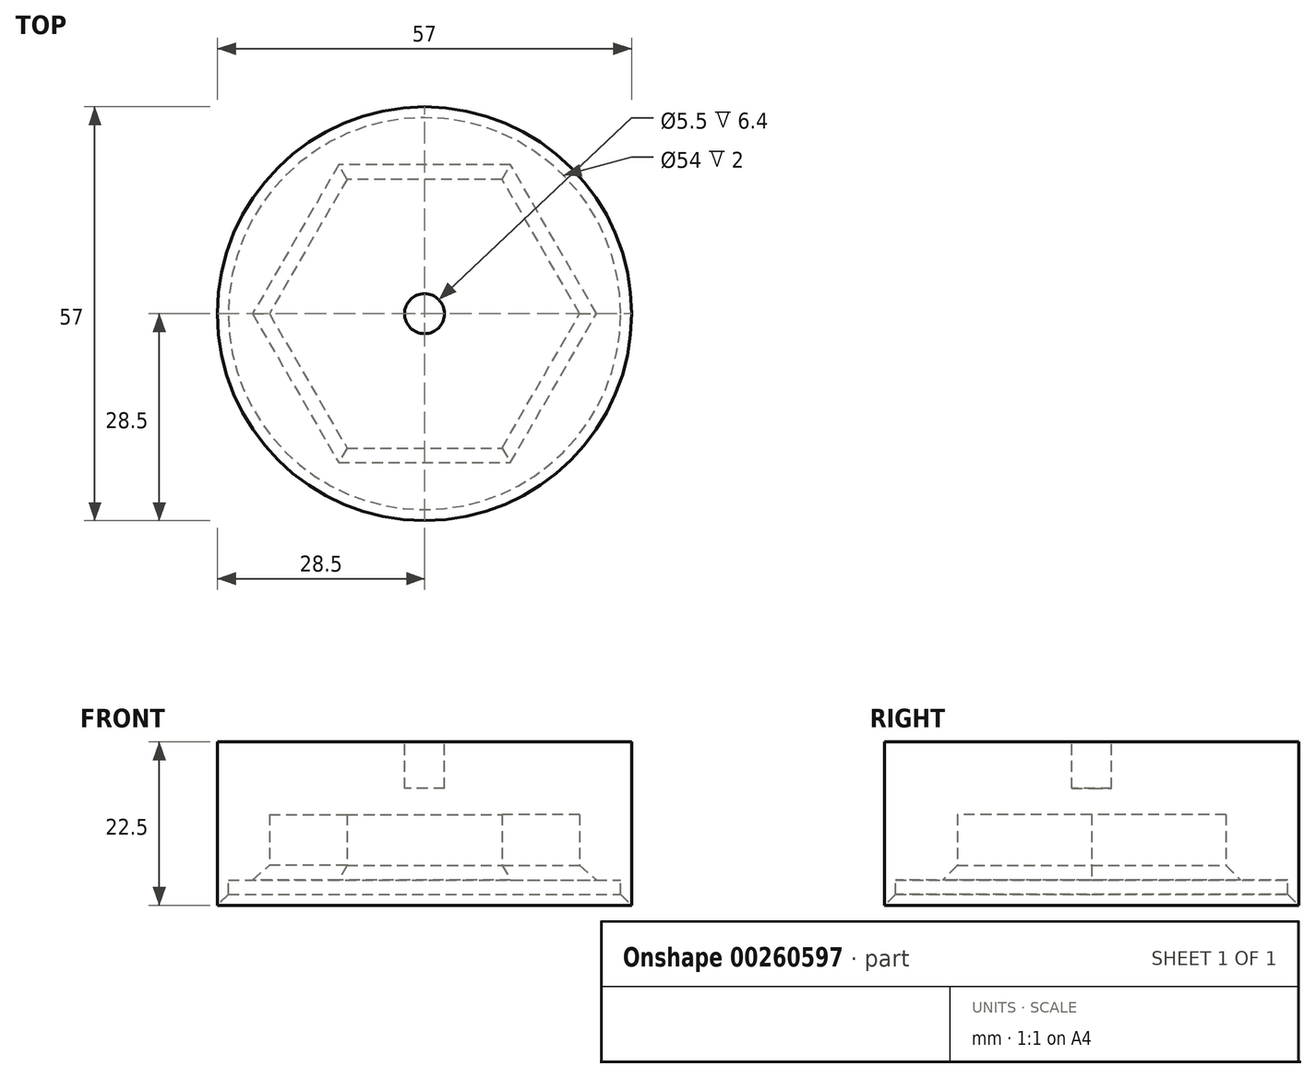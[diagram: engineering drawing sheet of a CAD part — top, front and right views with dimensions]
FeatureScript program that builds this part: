
annotation { "Feature Type Name" : "Feature", "Feature Type Description" : "" }
export const myFeature = defineFeature(function(context is Context, id is Id, definition is map)
    precondition{}
    {
        {
            var Q0;
            Q0=qCreatedBy(makeId("Top.planeOp"),FACE);
            var sketch = newSketch(context, id + "F0", { "sketchPlane" : qUnion([Q0])});
            skCircle(sketch, "E0", {"center": v(0, 0) * mm, "radius": 28.5 * mm});
            skSolve(sketch);
        }
        {
            var Q0;
            Q0=makeQuery(id+"F0.imprint","IMPRINT",FACE,{"disambiguationData":[TD([[makeQuery(id+"F0.imprint","IMPRINT",EDGE,{"derivedFrom":sQuery(id+"F0.wireOp",EDGE,"E0")}),1.0]])]});
            extrude(context, id + "F1", {"entities" : qUnion([Q0]), "depth" : 11 * mm, "offsetDistance" : 25 * mm});
        }
        {
            var Q0;
            Q0=makeQuery(id+"F1.opExtrude","CAP_FACE",FACE,{"disambiguationData":[OSD([sQuery(id+"F0.wireOp",EDGE,"E0")])],"isStart":true});
            var sketch = newSketch(context, id + "F2", { "sketchPlane" : qUnion([Q0])});
            skCircle(sketch, "E1.cCircle", {"center": v(0, 0) * mm, "radius": 18.5 * mm, "construction": true});
            skLineSegment(sketch, "E1.0", {"start": v(-10.68, 18.5) * mm, "end": v(10.68, 18.5) * mm});
            skLineSegment(sketch, "E1.1", {"start": v(10.68, 18.5) * mm, "end": v(21.36, 0) * mm});
            skLineSegment(sketch, "E1.2", {"start": v(21.36, 0) * mm, "end": v(10.68, -18.5) * mm});
            skLineSegment(sketch, "E1.3", {"start": v(10.68, -18.5) * mm, "end": v(-10.68, -18.5) * mm});
            skLineSegment(sketch, "E1.4", {"start": v(-10.68, -18.5) * mm, "end": v(-21.36, 0) * mm});
            skLineSegment(sketch, "E1.5", {"start": v(-21.36, 0) * mm, "end": v(-10.68, 18.5) * mm});
            skPoint(sketch, "E1.0.midPoint", {"position": v(0, 18.5) * mm});
            skSolve(sketch);
        }
        {
            var Q0;
            Q0=makeQuery(id+"F2.imprint","IMPRINT",FACE,{"disambiguationData":[TD([[makeQuery(id+"F2.imprint","IMPRINT",EDGE,{"derivedFrom":sQuery(id+"F2.wireOp",EDGE,"E1.0")}),-1.0]])]});
            extrude(context, id + "F3", {"entities" : qUnion([Q0]), "operationType" : NewBodyOperationType.REMOVE, "oppositeDirection" : true, "depth" : 1 * mm, "offsetDistance" : 25 * mm});
        }
        {
            var Q0;
            Q0=makeQuery(id+"F1.opExtrude","CAP_FACE",FACE,{"disambiguationData":[OSD([sQuery(id+"F0.wireOp",EDGE,"E0")])],"isStart":false});
            var sketch = newSketch(context, id + "F4", { "sketchPlane" : qUnion([Q0])});
            skCircle(sketch, "E2", {"center": v(0, 0) * mm, "radius": 2.75 * mm});
            skSolve(sketch);
        }
        {
            var Q0;
            Q0=makeQuery(id+"F4.imprint","IMPRINT",FACE,{"disambiguationData":[TD([[makeQuery(id+"F4.imprint","IMPRINT",EDGE,{"derivedFrom":sQuery(id+"F4.wireOp",EDGE,"E2")}),1.0]])]});
            extrude(context, id + "F5", {"entities" : qUnion([Q0]), "operationType" : NewBodyOperationType.REMOVE, "oppositeDirection" : true, "depth" : 6.4 * mm});
        }
        {
            var Q0;
            Q0=makeQuery(id+"F1.opExtrude","CAP_FACE",FACE,{"disambiguationData":[OSD([sQuery(id+"F0.wireOp",EDGE,"E0")])],"isStart":true});
            extrude(context, id + "F6", {"entities" : qUnion([Q0]), "operationType" : NewBodyOperationType.ADD, "depth" : 8 * mm, "offsetDistance" : 25 * mm});
        }
        {
            var Q0;
            Q0=makeQuery(id+"F6.opExtrude","CAP_FACE",FACE,{"disambiguationData":[OSD([sQuery(id+"F0.wireOp",EDGE,"E0")])],"isStart":false});
            var sketch = newSketch(context, id + "F7", { "sketchPlane" : qUnion([Q0])});
            skPoint(sketch, "E3.0", {"position": v(0, 0) * mm});
            skCircle(sketch, "E4", {"center": v(0, 0) * mm, "radius": 27 * mm});
            skSolve(sketch);
        }
        {
            var Q0;
            Q0=makeQuery(id+"F7.imprint","IMPRINT",FACE,{"disambiguationData":[TD([[makeQuery(id+"F7.imprint","IMPRINT",EDGE,{"derivedFrom":sQuery(id+"F7.wireOp",EDGE,"E4")}),-1.0]])]});
            extrude(context, id + "F8", {"entities" : qUnion([Q0]), "operationType" : NewBodyOperationType.ADD, "depth" : 4 * mm});
        }
        {
            var Q0;
            Q0=makeQuery(id+"F8.opExtrude","CAP_EDGE",EDGE,{"disambiguationData":[OSD([sQuery(id+"F7.wireOp",EDGE,"E4")])],"isStart":false});
            chamfer(context, id + "F9", {"entities" : qUnion([Q0]), "width" : 2 * mm, "tangentPropagation" : true});
        }
        {
            var Q0;
            Q0=makeQuery(id+"F6.opExtrude","CAP_EDGE",EDGE,{"disambiguationData":[OSD([sQuery(id+"F2.wireOp",EDGE,"E1.0")])],"isStart":false});
            var Q1;
            Q1=makeQuery(id+"F6.opExtrude","CAP_EDGE",EDGE,{"disambiguationData":[OSD([sQuery(id+"F2.wireOp",EDGE,"E1.1")])],"isStart":false});
            var Q2;
            Q2=makeQuery(id+"F6.opExtrude","CAP_EDGE",EDGE,{"disambiguationData":[OSD([sQuery(id+"F2.wireOp",EDGE,"E1.2")])],"isStart":false});
            var Q3;
            Q3=makeQuery(id+"F6.opExtrude","CAP_EDGE",EDGE,{"disambiguationData":[OSD([sQuery(id+"F2.wireOp",EDGE,"E1.3")])],"isStart":false});
            var Q4;
            Q4=makeQuery(id+"F6.opExtrude","CAP_EDGE",EDGE,{"disambiguationData":[OSD([sQuery(id+"F2.wireOp",EDGE,"E1.4")])],"isStart":false});
            var Q5;
            Q5=makeQuery(id+"F6.opExtrude","CAP_EDGE",EDGE,{"disambiguationData":[OSD([sQuery(id+"F2.wireOp",EDGE,"E1.5")])],"isStart":false});
            chamfer(context, id + "F10", {"entities" : qUnion([Q0, Q1, Q2, Q3, Q4, Q5]), "width" : 2 * mm, "tangentPropagation" : true});
        }
    });
